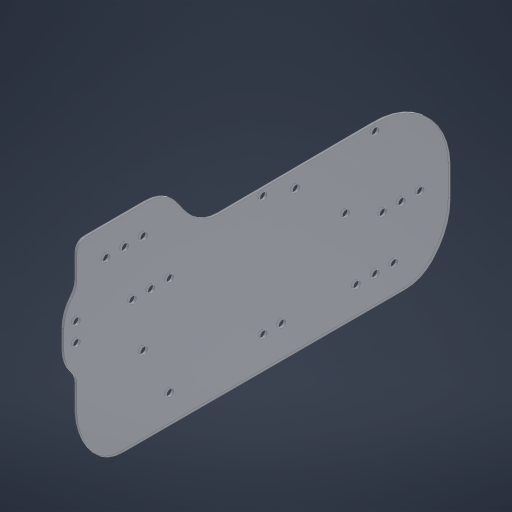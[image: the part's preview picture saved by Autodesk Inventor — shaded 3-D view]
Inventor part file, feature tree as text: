
AUTODESK INVENTOR PART (.ipt)
format: ipt  version: 2024 (Build 280153000, 153)  size: 340,992 bytes
history: native  units: in
note: dims shown in document units (in); Inventor stores cm internally (conversion verified against a paired STEP export)
features: sketch x1, extrude x1, hole x1
ambient origin geometry x8: Origin, YZ Plane, XZ Plane, XY Plane, X Axis, Y Axis, Z Axis, Center Point
bodies: Solid1 (feature_tree)
feature tree (3):
  sketch  "Sketch1"  dims[d4=0.0625in d5=0.0in d81=1.325in d82=1.5in d83=1.325in d84=1.5in d85=1.5in d88=0.5in d89=0.5in d90=0.5in d91=0.5in d92=1.0in d93=1.0in d94=1.5in d95=1.5in d96=0.5in d97=0.5in d98=1.325in d99=1.5in d100=0.5in d101=0.5in d102=0.1875in d103=0.75in d104=0.375in d105=0.25in d106=0.5635in d107=1.0in d108=0.8108in d109=1.5in d110=1.5in d111=0.25in d112=0.25in d122=0.75in d123=2.5in d124=7.5in d125=4.0in d126=1.5in d127=4.0in d128=1.5in d129=1.5in d130=0.875in d131=0.875in d132=1.723in d133=1.972in d134=1.0in d135=1.25in d136=2.875in d137=3.934in d138=1.0in d139=2.46in d140=1.0in d141=0.25in d142=0.35in d143=0.35in d144=0.5in d145=0.75in d146=0.75in d147=1.0in d148=1.0in d149=0.5in d150=1.0in d151=0.25in d152=1.5in d153=0.0625in d154=3.0in d155=1.0in d159=0.1in d160=0.2in d161=0.875in d162=1.51in d163=0.793in]
  extrude  "Extrusion1"  Depth=1.0in
  hole  "Hole4"  [1 undecoded]
note: 1 required parameter value undecoded (feature->parameter linkage not recoverable at this tier; creation-order binding heuristic only, values carry confidence <= 0.55)
